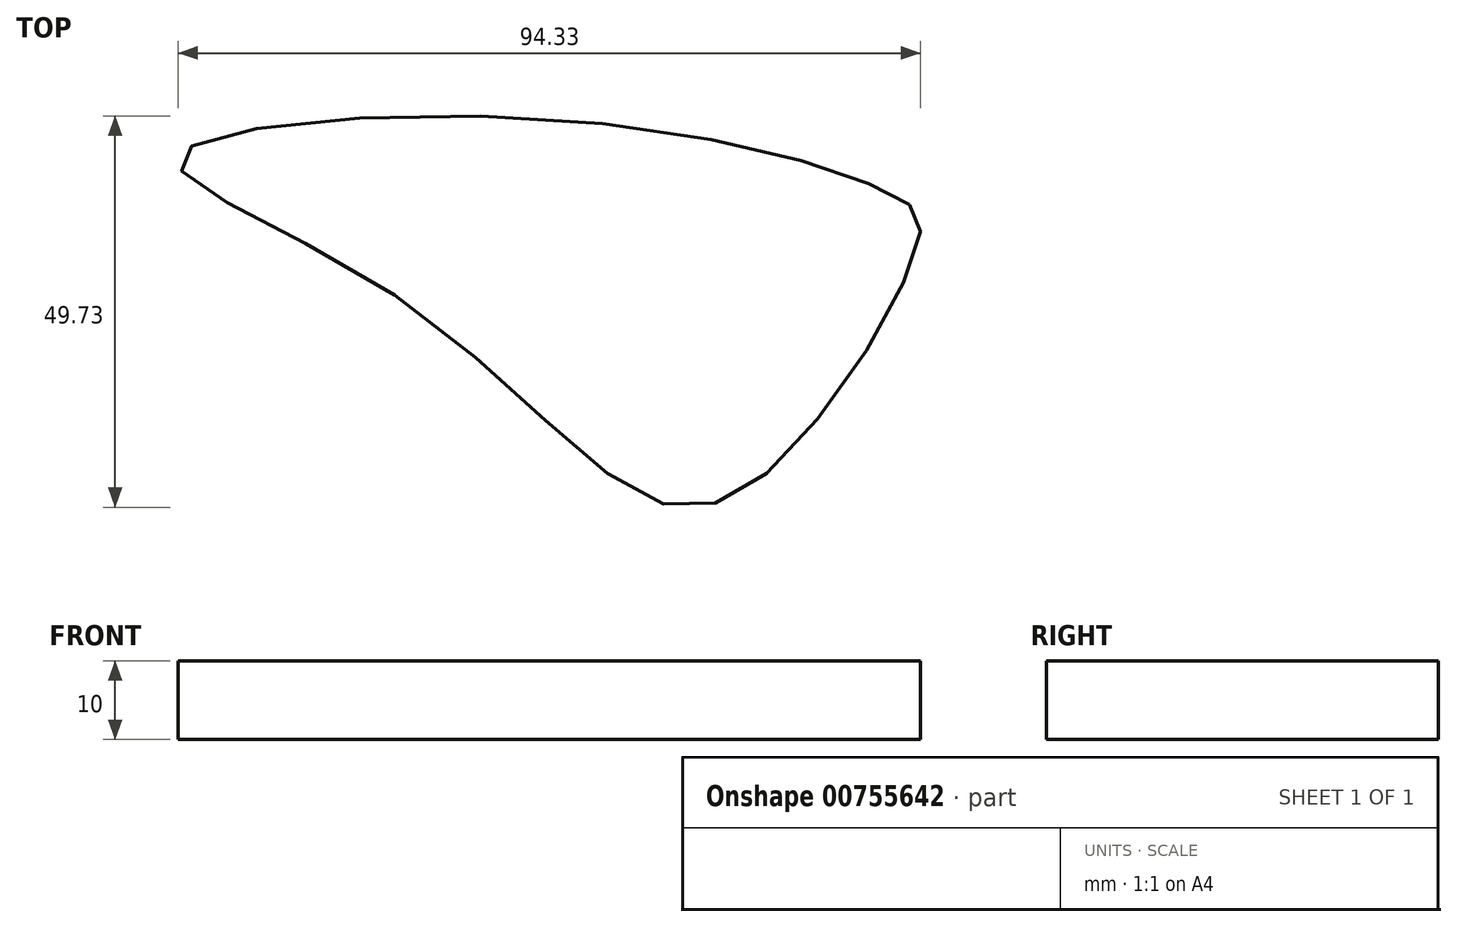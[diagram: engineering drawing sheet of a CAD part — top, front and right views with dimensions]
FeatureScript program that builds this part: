
annotation { "Feature Type Name" : "Feature", "Feature Type Description" : "" }
export const myFeature = defineFeature(function(context is Context, id is Id, definition is map)
    precondition{}
    {
        {
            var Q0;
            Q0=qCreatedBy(makeId("Top.planeOp"),FACE);
            var sketch = newSketch(context, id + "F0", { "sketchPlane" : qUnion([Q0])});
            skFitSpline(sketch, "E0", {"points": [v(-33.84, 26.45) * mm, v(-61.33, 43.7) * mm, v(-12.04, 48.63) * mm, v(30.24, 38.77) * mm, v(32.9, 34.22) * mm, v(16.97, 7.3) * mm, v(0, 0) * mm, v(-33.84, 26.45) * mm]});
            skSolve(sketch);
        }
        {
            var Q0;
            Q0=makeQuery(id+"F0.imprint","IMPRINT",FACE,{"disambiguationData":[TD([[makeQuery(id+"F0.imprint","IMPRINT",EDGE,{"derivedFrom":sQuery(id+"F0.wireOp",EDGE,"E0")}),-1.0]])]});
            extrude(context, id + "F1", {"entities" : qUnion([Q0]), "depth" : 10 * mm, "offsetDistance" : 25.4 * mm});
        }
    });
